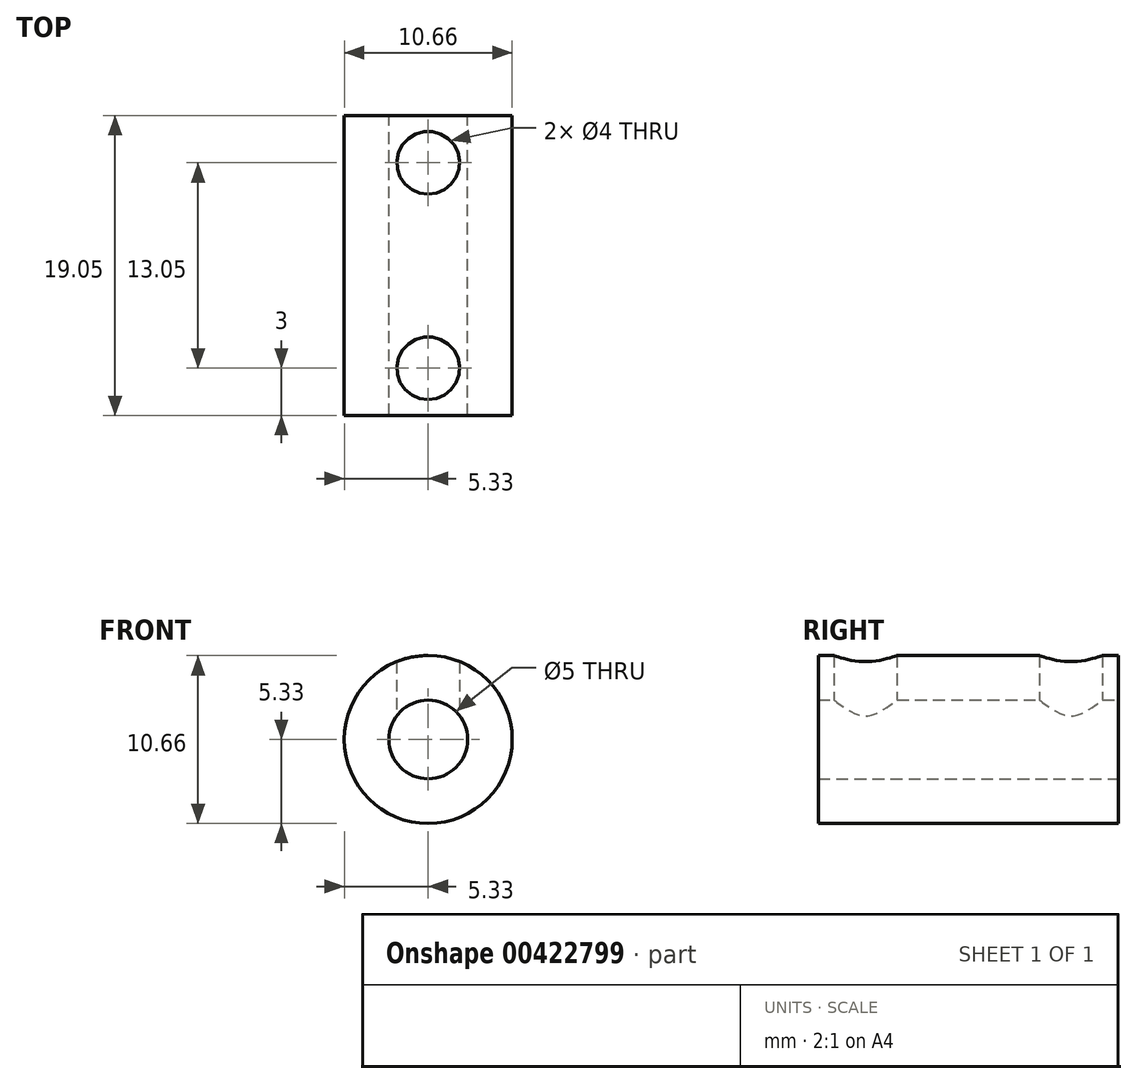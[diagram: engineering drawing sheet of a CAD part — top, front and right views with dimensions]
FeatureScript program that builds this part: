
annotation { "Feature Type Name" : "Feature", "Feature Type Description" : "" }
export const myFeature = defineFeature(function(context is Context, id is Id, definition is map)
    precondition{}
    {
        {
            var Q0;
            Q0=qCreatedBy(makeId("Front.planeOp"),FACE);
            var sketch = newSketch(context, id + "F0", { "sketchPlane" : qUnion([Q0])});
            skCircle(sketch, "E0", {"center": v(0, 0) * mm, "radius": 5.33 * mm});
            skCircle(sketch, "E1", {"center": v(0, 0) * mm, "radius": 2.5 * mm});
            skSolve(sketch);
        }
        {
            var Q0;
            Q0=makeQuery(id+"F0.imprint","IMPRINT",FACE,{"disambiguationData":[TD([[makeQuery(id+"F0.imprint","IMPRINT",EDGE,{"derivedFrom":sQuery(id+"F0.wireOp",EDGE,"E0")}),1.0]])]});
            extrude(context, id + "F1", {"entities" : qUnion([Q0]), "depth" : 19.05 * mm});
        }
        {
            var Q0;
            Q0=qCreatedBy(makeId("Top.planeOp"),FACE);
            var sketch = newSketch(context, id + "F2", { "sketchPlane" : qUnion([Q0])});
            skCircle(sketch, "E2", {"center": v(0, -3) * mm, "radius": 2 * mm});
            skLineSegment(sketch, "E3", {"start": v(0, -1) * mm, "end": v(0, 0) * mm});
            skCircle(sketch, "E4", {"center": v(0, -16.05) * mm, "radius": 2 * mm});
            skLineSegment(sketch, "E5", {"start": v(0, -18.05) * mm, "end": v(0, -19.05) * mm});
            skSolve(sketch);
        }
        {
            var Q0;
            Q0=makeQuery(id+"F2.imprint","IMPRINT",FACE,{"disambiguationData":[TD([[makeQuery(id+"F2.imprint","IMPRINT",EDGE,{"derivedFrom":sQuery(id+"F2.wireOp",EDGE,"E4")}),1.0]])]});
            var Q1;
            Q1=makeQuery(id+"F2.imprint","IMPRINT",FACE,{"disambiguationData":[TD([[makeQuery(id+"F2.imprint","IMPRINT",EDGE,{"derivedFrom":sQuery(id+"F2.wireOp",EDGE,"E2")}),1.0]])]});
            extrude(context, id + "F3", {"entities" : qUnion([Q0, Q1]), "operationType" : NewBodyOperationType.REMOVE, "depth" : 25.4 * mm});
        }
        {
            var Q0;
            Q0=qCreatedBy(makeId("Top.planeOp"),FACE);
            var sketch = newSketch(context, id + "F4", { "sketchPlane" : qUnion([Q0])});
            skLineSegment(sketch, "E6", {"start": v(0, 0) * mm, "end": v(0, -19.05) * mm});
            skPoint(sketch, "E7", {"position": v(0, -9.53) * mm});
            skSolve(sketch);
        }
    });
